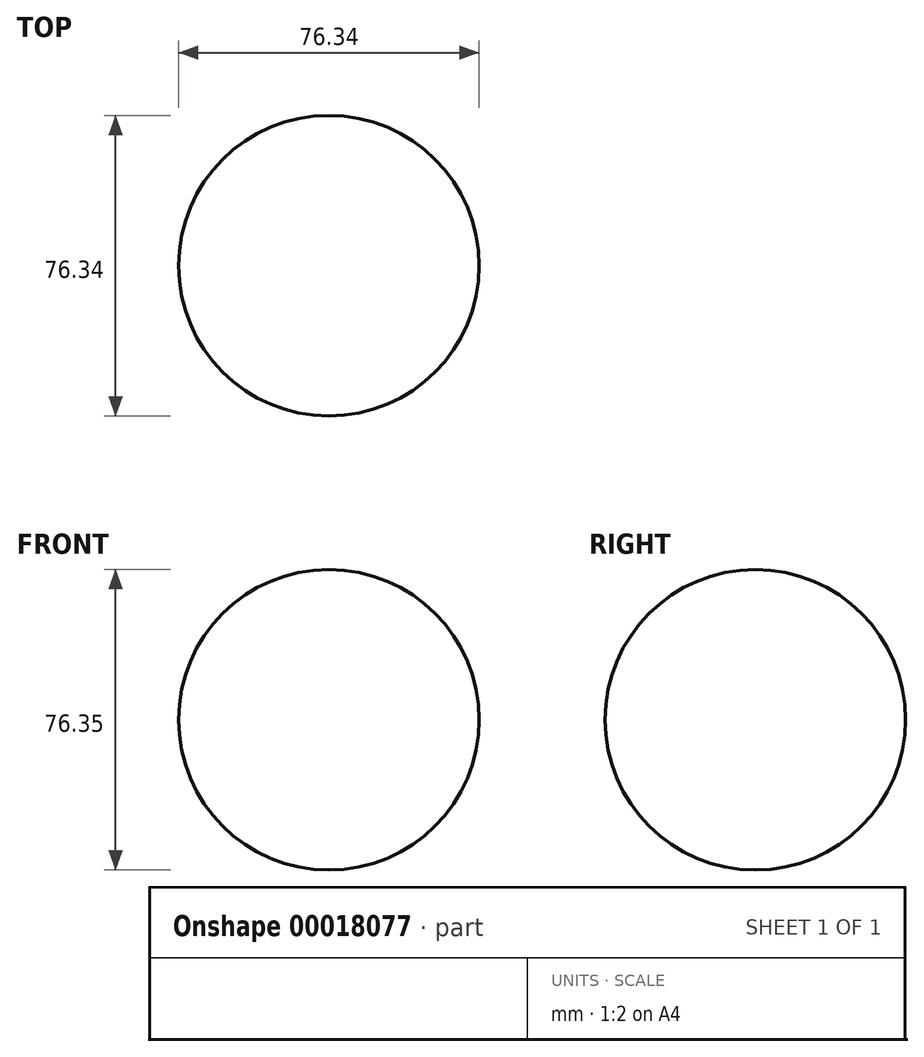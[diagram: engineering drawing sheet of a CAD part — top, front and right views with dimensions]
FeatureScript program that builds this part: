
annotation { "Feature Type Name" : "Feature", "Feature Type Description" : "" }
export const myFeature = defineFeature(function(context is Context, id is Id, definition is map)
    precondition{}
    {
        {
            var Q0;
            Q0=qCreatedBy(makeId("Top.planeOp"),FACE);
            var sketch = newSketch(context, id + "F0", { "sketchPlane" : qUnion([Q0])});
            skCircle(sketch, "E0", {"center": v(0, 0) * mm, "radius": 38.1 * mm});
            skSolve(sketch);
        }
        {
            var Q0;
            Q0=qCreatedBy(makeId("Top.planeOp"),FACE);
            cPlane(context, id + "F1", {"entities" : qUnion([Q0]), "cplaneType" : CPlaneType.OFFSET, "offset" : 76.2 * mm, "width" : 152.4 * mm, "height" : 152.4 * mm});
        }
        {
            var Q0;
            Q0=qCreatedBy(makeId("Front.planeOp"),FACE);
            var sketch = newSketch(context, id + "F2", { "sketchPlane" : qUnion([Q0])});
            skLineSegment(sketch, "E1", {"start": v(0, 0) * mm, "end": v(0, 76.35) * mm});
            skCircle(sketch, "E2", {"center": v(0, 38.17) * mm, "radius": 38.17 * mm});
            skSolve(sketch);
        }
        {
            var Q0;
            {var subQ1=sQuery(id+"F2.wireOp",EDGE,"E1");Q0=makeQuery(id+"F2.imprint","IMPRINT",FACE,{"disambiguationData":[TD([[makeQuery(id+"F2.imprint","IMPRINT",EDGE,{"derivedFrom":subQ1}),1.0]])]});}
            var Q1;
            Q1=sQuery(id+"F2.wireOp",EDGE,"E1");
            revolve(context, id + "F3", {"entities" : qUnion([Q0]), "axis" : qUnion([Q1]), "revolveType" : RevolveType.FULL});
        }
    });
